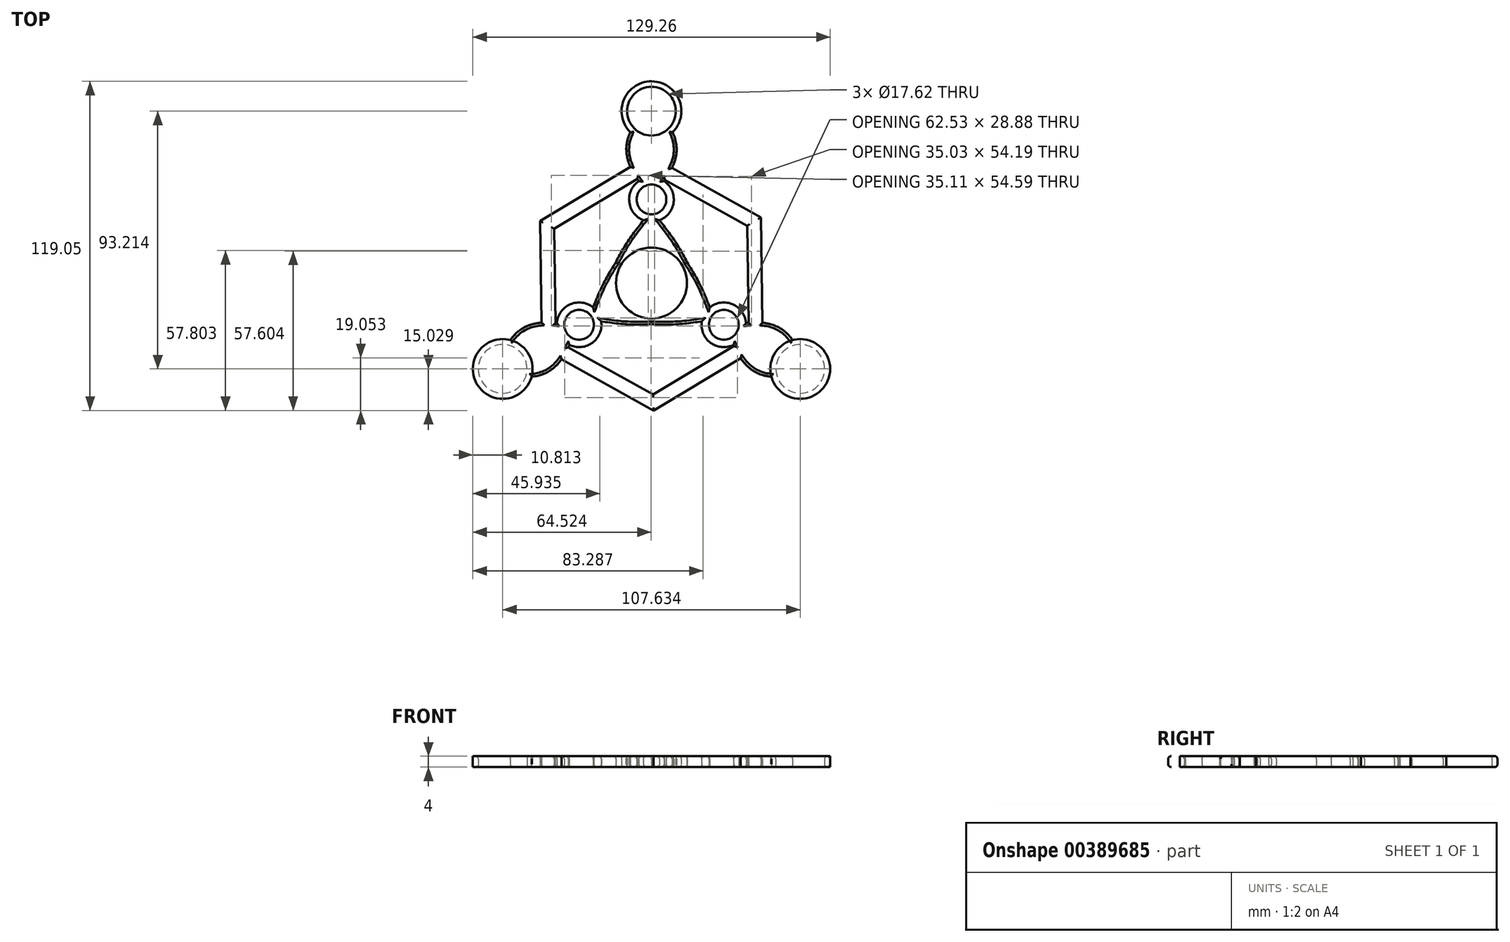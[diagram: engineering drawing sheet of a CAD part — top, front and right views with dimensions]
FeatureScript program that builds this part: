
annotation { "Feature Type Name" : "Feature", "Feature Type Description" : "" }
export const myFeature = defineFeature(function(context is Context, id is Id, definition is map)
    precondition{}
    {
        {
            var Q0;
            Q0=qCreatedBy(makeId("Top.planeOp"),FACE);
            var sketch = newSketch(context, id + "F0", { "sketchPlane" : qUnion([Q0])});
            skCircle(sketch, "E0", {"center": v(0, 0) * mm, "radius": 14.84 * mm});
            skCircle(sketch, "E1", {"center": v(0, 62.14) * mm, "radius": 10.8 * mm});
            skFitSpline(sketch, "E2", {"points": [v(-13.39, 6.4) * mm, v(0, 30.23) * mm, v(-7.64, 54.5) * mm], "startDerivative": vector(48.16, 100) * mm, "endDerivative": vector(32.63, 68.5) * mm});
            skFitSpline(sketch, "E3.MirrorCS", {"points": [v(13.39, 6.4) * mm, v(0, 30.23) * mm, v(7.64, 54.5) * mm], "startDerivative": vector(-48.16, 100) * mm, "endDerivative": vector(-32.63, 68.5) * mm});
            skCircle(sketch, "E4", {"center": v(0, 30.23) * mm, "radius": 5.38 * mm});
            skArc(sketch, "E5.0", {"start": v(-4.57, 36.9) * mm, "mid": v(-8.02, 29.28) * mm, "end": v(-2.88, 22.68) * mm});
            skFitSpline(sketch, "E6.trimOffspring", {"points": [v(13.39, 6.4) * mm, v(0, 30.23) * mm, v(7.64, 54.5) * mm], "startDerivative": vector(-48.16, 100) * mm, "endDerivative": vector(-32.63, 68.5) * mm});
            skLineSegment(sketch, "E7.trimOffspring", {"start": v(0, 30.23) * mm, "end": v(0, 30.23) * mm});
            skArc(sketch, "E8.trimOffspring", {"start": v(2.88, 22.68) * mm, "mid": v(8.02, 29.28) * mm, "end": v(4.57, 36.9) * mm});
            skCircle(sketch, "E9.1.0", {"center": v(-53.82, -31.07) * mm, "radius": 10.8 * mm});
            skCircle(sketch, "E9.2.0", {"center": v(53.82, -31.07) * mm, "radius": 10.8 * mm});
            skCircle(sketch, "E10.0", {"center": v(0, 0) * mm, "radius": 12.84 * mm});
            skCircle(sketch, "E11.0", {"center": v(0, 62.14) * mm, "radius": 8.8 * mm});
            skSolve(sketch);
        }
        {
            var Q0;
            Q0 = qSketchRegion(id + "F0", true);
            extrude(context, id + "F1", {"entities" : qUnion([Q0]), "depth" : 4 * mm});
        }
        {
            var Q0;
            Q0=makeQuery(id+"F1.opExtrude","SWEPT_BODY",BODY,{"disambiguationData":[OSD([sQuery(id+"F0.wireOp",EDGE,"E0"),sQuery(id+"F0.wireOp",EDGE,"E1"),sQuery(id+"F0.wireOp",EDGE,"E2"),sQuery(id+"F0.wireOp",EDGE,"E3.MirrorCS"),sQuery(id+"F0.wireOp",EDGE,"E4"),sQuery(id+"F0.wireOp",EDGE,"E5.0"),sQuery(id+"F0.wireOp",EDGE,"E6.trimOffspring"),sQuery(id+"F0.wireOp",EDGE,"E2"),sQuery(id+"F0.wireOp",EDGE,"E8.trimOffspring"),sQuery(id+"F0.wireOp",EDGE,"E10.0"),sQuery(id+"F0.wireOp",EDGE,"E11.0")])]});
            var Q1;
            Q1=makeQuery(id+"F1.opExtrude","CAP_EDGE",EDGE,{"disambiguationData":[OSD([sQuery(id+"F0.wireOp",EDGE,"E10.0")])],"isStart":false});
            circularPattern(context, id + "F2", {"entities" : qUnion([Q0]), "axis" : qUnion([Q1]), "angle" : 360 * degree, "instanceCount" : 3, "equalSpace" : true});
        }
        {
            var Q0;
            Q0=qCreatedBy(makeId("Top.planeOp"),FACE);
            var sketch = newSketch(context, id + "F3", { "sketchPlane" : qUnion([Q0])});
            skCircle(sketch, "E12.cCircle", {"center": v(0, 0) * mm, "radius": 39.93 * mm, "construction": true});
            skLineSegment(sketch, "E12.0", {"start": v(0.71, -46.1) * mm, "end": v(-39.57, -23.67) * mm});
            skLineSegment(sketch, "E12.1", {"start": v(-39.57, -23.67) * mm, "end": v(-40.28, 22.43) * mm});
            skLineSegment(sketch, "E12.2", {"start": v(-40.28, 22.43) * mm, "end": v(-0.71, 46.1) * mm});
            skLineSegment(sketch, "E12.3", {"start": v(-0.71, 46.1) * mm, "end": v(39.57, 23.67) * mm});
            skLineSegment(sketch, "E12.4", {"start": v(39.57, 23.67) * mm, "end": v(40.28, -22.43) * mm});
            skLineSegment(sketch, "E12.5", {"start": v(40.28, -22.43) * mm, "end": v(0.71, -46.1) * mm});
            skPoint(sketch, "E12.0.midPoint", {"position": v(-19.43, -34.89) * mm});
            skLineSegment(sketch, "E13.0", {"start": v(-0.63, 40.33) * mm, "end": v(34.61, 20.7) * mm});
            skLineSegment(sketch, "E13.1", {"start": v(35.24, -19.62) * mm, "end": v(0.63, -40.33) * mm});
            skLineSegment(sketch, "E13.2", {"start": v(0.63, -40.33) * mm, "end": v(-34.61, -20.7) * mm});
            skLineSegment(sketch, "E13.3", {"start": v(34.61, 20.7) * mm, "end": v(35.24, -19.62) * mm});
            skLineSegment(sketch, "E13.4", {"start": v(-34.61, -20.7) * mm, "end": v(-35.24, 19.62) * mm});
            skLineSegment(sketch, "E13.5", {"start": v(-35.24, 19.62) * mm, "end": v(-0.63, 40.33) * mm});
            skSolve(sketch);
        }
        {
            var Q0;
            Q0=makeQuery(id+"F3.imprint","IMPRINT",FACE,{"disambiguationData":[TD([[makeQuery(id+"F3.imprint","IMPRINT",EDGE,{"derivedFrom":sQuery(id+"F3.wireOp",EDGE,"E12.0")}),-1.0]])]});
            extrude(context, id + "F4", {"entities" : qUnion([Q0]), "operationType" : NewBodyOperationType.ADD, "depth" : 4 * mm});
        }
        {
            var Q0;
            {var subQ0=makeQuery(id+"F1.opExtrude","CAP_FACE",FACE,{"disambiguationData":[OSD([sQuery(id+"F0.wireOp",EDGE,"E0"),sQuery(id+"F0.wireOp",EDGE,"E1"),sQuery(id+"F0.wireOp",EDGE,"E2"),sQuery(id+"F0.wireOp",EDGE,"E3.MirrorCS"),sQuery(id+"F0.wireOp",EDGE,"E4"),sQuery(id+"F0.wireOp",EDGE,"E5.0"),sQuery(id+"F0.wireOp",EDGE,"E6.trimOffspring"),sQuery(id+"F0.wireOp",EDGE,"E2"),sQuery(id+"F0.wireOp",EDGE,"E8.trimOffspring"),sQuery(id+"F0.wireOp",EDGE,"E10.0"),sQuery(id+"F0.wireOp",EDGE,"E11.0")])],"isStart":false});Q0=makeQuery(id+"F4.boolean.opBoolean","MERGE",FACE,{"derivedFrom":[subQ0,makeQuery(id+"F2.opPattern","COPY",FACE,{"derivedFrom":subQ0,"instanceName":"1"}),makeQuery(id+"F2.opPattern","COPY",FACE,{"derivedFrom":subQ0,"instanceName":"2"}),makeQuery(id+"F4.opExtrude","CAP_FACE",FACE,{"disambiguationData":[OSD([sQuery(id+"F3.wireOp",EDGE,"E12.0"),sQuery(id+"F3.wireOp",EDGE,"E12.1"),sQuery(id+"F3.wireOp",EDGE,"E12.2"),sQuery(id+"F3.wireOp",EDGE,"E12.3"),sQuery(id+"F3.wireOp",EDGE,"E12.4"),sQuery(id+"F3.wireOp",EDGE,"E12.5"),sQuery(id+"F3.wireOp",EDGE,"E13.0"),sQuery(id+"F3.wireOp",EDGE,"E13.1"),sQuery(id+"F3.wireOp",EDGE,"E13.2"),sQuery(id+"F3.wireOp",EDGE,"E13.3"),sQuery(id+"F3.wireOp",EDGE,"E13.4"),sQuery(id+"F3.wireOp",EDGE,"E13.5")])],"isStart":false})]});}
            var Q1;
            {var subQ0=makeQuery(id+"F1.opExtrude","CAP_FACE",FACE,{"disambiguationData":[OSD([sQuery(id+"F0.wireOp",EDGE,"E0"),sQuery(id+"F0.wireOp",EDGE,"E1"),sQuery(id+"F0.wireOp",EDGE,"E2"),sQuery(id+"F0.wireOp",EDGE,"E3.MirrorCS"),sQuery(id+"F0.wireOp",EDGE,"E4"),sQuery(id+"F0.wireOp",EDGE,"E5.0"),sQuery(id+"F0.wireOp",EDGE,"E6.trimOffspring"),sQuery(id+"F0.wireOp",EDGE,"E2"),sQuery(id+"F0.wireOp",EDGE,"E8.trimOffspring"),sQuery(id+"F0.wireOp",EDGE,"E10.0"),sQuery(id+"F0.wireOp",EDGE,"E11.0")])],"isStart":true});Q1=makeQuery(id+"F4.boolean.opBoolean","MERGE",FACE,{"derivedFrom":[subQ0,makeQuery(id+"F2.opPattern","COPY",FACE,{"derivedFrom":subQ0,"instanceName":"1"}),makeQuery(id+"F2.opPattern","COPY",FACE,{"derivedFrom":subQ0,"instanceName":"2"}),makeQuery(id+"F4.opExtrude","CAP_FACE",FACE,{"disambiguationData":[OSD([sQuery(id+"F3.wireOp",EDGE,"E12.0"),sQuery(id+"F3.wireOp",EDGE,"E12.1"),sQuery(id+"F3.wireOp",EDGE,"E12.2"),sQuery(id+"F3.wireOp",EDGE,"E12.3"),sQuery(id+"F3.wireOp",EDGE,"E12.4"),sQuery(id+"F3.wireOp",EDGE,"E12.5"),sQuery(id+"F3.wireOp",EDGE,"E13.0"),sQuery(id+"F3.wireOp",EDGE,"E13.1"),sQuery(id+"F3.wireOp",EDGE,"E13.2"),sQuery(id+"F3.wireOp",EDGE,"E13.3"),sQuery(id+"F3.wireOp",EDGE,"E13.4"),sQuery(id+"F3.wireOp",EDGE,"E13.5")])],"isStart":true})]});}
            fillet(context, id + "F5", {"entities" : qUnion([Q0, Q1]), "radius" : 1 * mm, "tangentPropagation" : true, "allowEdgeOverflow" : false});
        }
    });
